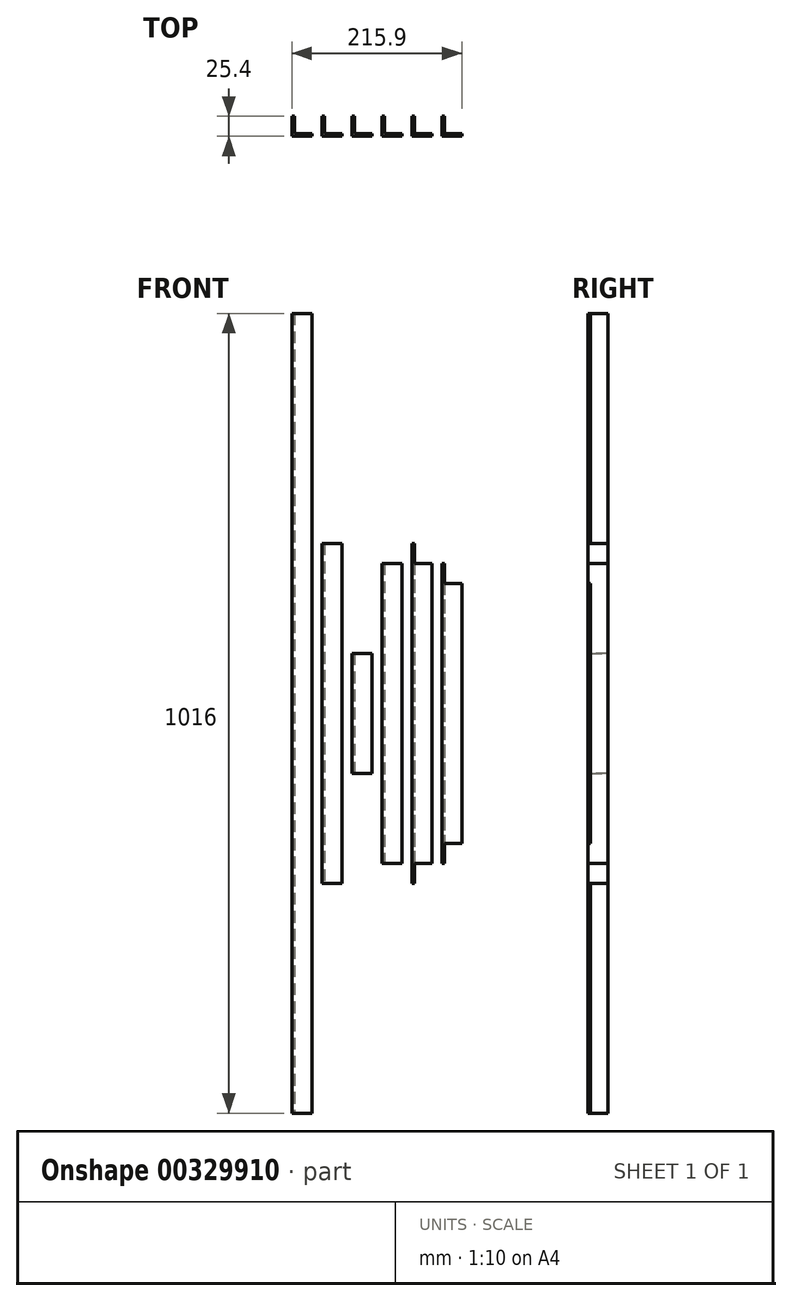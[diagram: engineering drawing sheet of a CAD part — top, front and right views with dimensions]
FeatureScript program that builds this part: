
annotation { "Feature Type Name" : "Feature", "Feature Type Description" : "" }
export const myFeature = defineFeature(function(context is Context, id is Id, definition is map)
    precondition{}
    {
        {
            var Q0;
            Q0=qCreatedBy(makeId("Top.planeOp"),FACE);
            var sketch = newSketch(context, id + "F0", { "sketchPlane" : qUnion([Q0])});
            skLineSegment(sketch, "E0", {"start": v(0, 25.4) * mm, "end": v(0, 0) * mm});
            skLineSegment(sketch, "E1", {"start": v(0, 0) * mm, "end": v(25.4, 0) * mm});
            skLineSegment(sketch, "E2", {"start": v(25.4, 0) * mm, "end": v(25.4, 3.18) * mm});
            skLineSegment(sketch, "E3", {"start": v(25.4, 3.18) * mm, "end": v(3.18, 3.17) * mm});
            skLineSegment(sketch, "E4", {"start": v(3.18, 3.17) * mm, "end": v(3.18, 25.4) * mm});
            skLineSegment(sketch, "E5", {"start": v(3.18, 25.4) * mm, "end": v(0, 25.4) * mm});
            skLineSegment(sketch, "E6.1.0.0", {"start": v(63.5, 3.18) * mm, "end": v(41.28, 3.17) * mm});
            skLineSegment(sketch, "E6.1.0.1", {"start": v(41.28, 3.17) * mm, "end": v(41.28, 25.4) * mm});
            skLineSegment(sketch, "E6.1.0.2", {"start": v(38.1, 0) * mm, "end": v(63.5, 0) * mm});
            skLineSegment(sketch, "E6.1.0.3", {"start": v(38.1, 25.4) * mm, "end": v(38.1, 0) * mm});
            skLineSegment(sketch, "E6.1.0.4", {"start": v(63.5, 0) * mm, "end": v(63.5, 3.18) * mm});
            skLineSegment(sketch, "E6.1.0.5", {"start": v(41.27, 25.4) * mm, "end": v(38.1, 25.4) * mm});
            skLineSegment(sketch, "E6.2.0.0", {"start": v(101.6, 3.18) * mm, "end": v(79.38, 3.17) * mm});
            skLineSegment(sketch, "E6.2.0.1", {"start": v(79.38, 3.17) * mm, "end": v(79.38, 25.4) * mm});
            skLineSegment(sketch, "E6.2.0.2", {"start": v(76.2, 0) * mm, "end": v(101.6, 0) * mm});
            skLineSegment(sketch, "E6.2.0.3", {"start": v(76.2, 25.4) * mm, "end": v(76.2, 0) * mm});
            skLineSegment(sketch, "E6.2.0.4", {"start": v(101.6, 0) * mm, "end": v(101.6, 3.18) * mm});
            skLineSegment(sketch, "E6.2.0.5", {"start": v(79.38, 25.4) * mm, "end": v(76.2, 25.4) * mm});
            skLineSegment(sketch, "E6.direction1", {"start": v(0, 0) * mm, "end": v(38.1, 0) * mm, "construction": true});
            skLineSegment(sketch, "E7.0.3.0", {"start": v(139.7, 3.18) * mm, "end": v(117.47, 3.17) * mm});
            skLineSegment(sketch, "E7.3.3.0", {"start": v(117.47, 3.17) * mm, "end": v(117.47, 25.4) * mm});
            skLineSegment(sketch, "E7.6.3.0", {"start": v(114.3, 0) * mm, "end": v(139.7, 0) * mm});
            skLineSegment(sketch, "E7.9.3.0", {"start": v(114.3, 25.4) * mm, "end": v(114.3, 0) * mm});
            skLineSegment(sketch, "E7.12.3.0", {"start": v(139.7, 0) * mm, "end": v(139.7, 3.18) * mm});
            skLineSegment(sketch, "E7.15.3.0", {"start": v(117.47, 25.4) * mm, "end": v(114.3, 25.4) * mm});
            skLineSegment(sketch, "E8.0.4.0", {"start": v(177.8, 3.18) * mm, "end": v(155.57, 3.17) * mm});
            skLineSegment(sketch, "E8.3.4.0", {"start": v(155.57, 3.17) * mm, "end": v(155.57, 25.4) * mm});
            skLineSegment(sketch, "E8.6.4.0", {"start": v(152.4, 0) * mm, "end": v(177.8, 0) * mm});
            skLineSegment(sketch, "E8.9.4.0", {"start": v(152.4, 25.4) * mm, "end": v(152.4, 0) * mm});
            skLineSegment(sketch, "E8.12.4.0", {"start": v(177.8, 0) * mm, "end": v(177.8, 3.18) * mm});
            skLineSegment(sketch, "E8.15.4.0", {"start": v(155.57, 25.4) * mm, "end": v(152.4, 25.4) * mm});
            skLineSegment(sketch, "E9.0.5.0", {"start": v(215.9, 3.18) * mm, "end": v(193.67, 3.17) * mm});
            skLineSegment(sketch, "E9.3.5.0", {"start": v(193.67, 3.17) * mm, "end": v(193.67, 25.4) * mm});
            skLineSegment(sketch, "E9.6.5.0", {"start": v(190.5, 0) * mm, "end": v(215.9, 0) * mm});
            skLineSegment(sketch, "E9.9.5.0", {"start": v(190.5, 25.4) * mm, "end": v(190.5, 0) * mm});
            skLineSegment(sketch, "E9.12.5.0", {"start": v(215.9, 0) * mm, "end": v(215.9, 3.18) * mm});
            skLineSegment(sketch, "E9.15.5.0", {"start": v(193.67, 25.4) * mm, "end": v(190.5, 25.4) * mm});
            skSolve(sketch);
        }
        {
            var Q0;
            Q0=makeQuery(id+"F0.imprint","IMPRINT",FACE,{"disambiguationData":[TD([[makeQuery(id+"F0.imprint","IMPRINT",EDGE,{"derivedFrom":sQuery(id+"F0.wireOp",EDGE,"E0")}),1.0]])]});
            extrude(context, id + "F1", {"entities" : qUnion([Q0]), "depth" : 1016 * mm, "symmetric" : true});
        }
        {
            var Q0;
            Q0=makeQuery(id+"F0.imprint","IMPRINT",FACE,{"disambiguationData":[TD([[makeQuery(id+"F0.imprint","IMPRINT",EDGE,{"derivedFrom":sQuery(id+"F0.wireOp",EDGE,"E6.1.0.0")}),1.0]])]});
            extrude(context, id + "F2", {"entities" : qUnion([Q0]), "depth" : 431.8 * mm, "symmetric" : true});
        }
        {
            var Q0;
            Q0=makeQuery(id+"F0.imprint","IMPRINT",FACE,{"disambiguationData":[TD([[makeQuery(id+"F0.imprint","IMPRINT",EDGE,{"derivedFrom":sQuery(id+"F0.wireOp",EDGE,"E6.2.0.0")}),1.0]])]});
            extrude(context, id + "F3", {"entities" : qUnion([Q0]), "depth" : 152.4 * mm, "symmetric" : true});
        }
        {
            var Q0;
            Q0=makeQuery(id+"F0.imprint","IMPRINT",FACE,{"disambiguationData":[TD([[makeQuery(id+"F0.imprint","IMPRINT",EDGE,{"derivedFrom":sQuery(id+"F0.wireOp",EDGE,"E7.0.3.0")}),1.0]])]});
            extrude(context, id + "F4", {"entities" : qUnion([Q0]), "depth" : 381 * mm, "symmetric" : true});
        }
        {
            var Q0;
            Q0=makeQuery(id+"F0.imprint","IMPRINT",FACE,{"disambiguationData":[TD([[makeQuery(id+"F0.imprint","IMPRINT",EDGE,{"derivedFrom":sQuery(id+"F0.wireOp",EDGE,"E8.0.4.0")}),1.0]])]});
            extrude(context, id + "F5", {"entities" : qUnion([Q0]), "depth" : 431.8 * mm, "symmetric" : true});
        }
        {
            var Q0;
            Q0=makeQuery(id+"F0.imprint","IMPRINT",FACE,{"disambiguationData":[TD([[makeQuery(id+"F0.imprint","IMPRINT",EDGE,{"derivedFrom":sQuery(id+"F0.wireOp",EDGE,"E9.0.5.0")}),1.0]])]});
            extrude(context, id + "F6", {"entities" : qUnion([Q0]), "depth" : 381 * mm, "symmetric" : true});
        }
        {
            var Q0;
            Q0=makeQuery(id+"F5.opExtrude","CAP_FACE",FACE,{"disambiguationData":[OSD([sQuery(id+"F0.wireOp",EDGE,"E8.0.4.0"),sQuery(id+"F0.wireOp",EDGE,"E8.3.4.0"),sQuery(id+"F0.wireOp",EDGE,"E8.6.4.0"),sQuery(id+"F0.wireOp",EDGE,"E8.9.4.0"),sQuery(id+"F0.wireOp",EDGE,"E8.12.4.0"),sQuery(id+"F0.wireOp",EDGE,"E8.15.4.0")])],"isStart":true});
            var sketch = newSketch(context, id + "F7", { "sketchPlane" : qUnion([Q0])});
            skLineSegment(sketch, "E10.bottom", {"start": v(155.57, -3.17) * mm, "end": v(177.8, -3.17) * mm});
            skLineSegment(sketch, "E10.top", {"start": v(155.57, 0) * mm, "end": v(177.8, 0) * mm});
            skLineSegment(sketch, "E10.left", {"start": v(155.57, -3.17) * mm, "end": v(155.57, 0) * mm});
            skLineSegment(sketch, "E10.right", {"start": v(177.8, -3.17) * mm, "end": v(177.8, 0) * mm});
            skSolve(sketch);
        }
        {
            var Q0;
            Q0=makeQuery(id+"F7.imprint","IMPRINT",FACE,{"disambiguationData":[TD([[makeQuery(id+"F7.imprint","IMPRINT",EDGE,{"derivedFrom":sQuery(id+"F7.wireOp",EDGE,"E10.bottom")}),-1.0]])]});
            extrude(context, id + "F8", {"entities" : qUnion([Q0]), "operationType" : NewBodyOperationType.REMOVE, "oppositeDirection" : true, "depth" : 25.4 * mm});
        }
        {
            var Q0;
            Q0=makeQuery(id+"F5.opExtrude","CAP_FACE",FACE,{"disambiguationData":[OSD([sQuery(id+"F0.wireOp",EDGE,"E8.0.4.0"),sQuery(id+"F0.wireOp",EDGE,"E8.3.4.0"),sQuery(id+"F0.wireOp",EDGE,"E8.6.4.0"),sQuery(id+"F0.wireOp",EDGE,"E8.9.4.0"),sQuery(id+"F0.wireOp",EDGE,"E8.12.4.0"),sQuery(id+"F0.wireOp",EDGE,"E8.15.4.0")])],"isStart":false});
            var sketch = newSketch(context, id + "F9", { "sketchPlane" : qUnion([Q0])});
            skLineSegment(sketch, "E11.bottom", {"start": v(155.57, 3.17) * mm, "end": v(177.8, 3.17) * mm});
            skLineSegment(sketch, "E11.top", {"start": v(155.57, 0) * mm, "end": v(177.8, 0) * mm});
            skLineSegment(sketch, "E11.left", {"start": v(155.57, 3.17) * mm, "end": v(155.57, 0) * mm});
            skLineSegment(sketch, "E11.right", {"start": v(177.8, 3.17) * mm, "end": v(177.8, 0) * mm});
            skSolve(sketch);
        }
        {
            var Q0;
            Q0=makeQuery(id+"F9.imprint","IMPRINT",FACE,{"disambiguationData":[TD([[makeQuery(id+"F9.imprint","IMPRINT",EDGE,{"derivedFrom":sQuery(id+"F9.wireOp",EDGE,"E11.bottom")}),1.0]])]});
            extrude(context, id + "F10", {"entities" : qUnion([Q0]), "operationType" : NewBodyOperationType.REMOVE, "oppositeDirection" : true, "depth" : 25.4 * mm});
        }
        {
            var Q0;
            Q0=makeQuery(id+"F6.opExtrude","CAP_FACE",FACE,{"disambiguationData":[OSD([sQuery(id+"F0.wireOp",EDGE,"E9.0.5.0"),sQuery(id+"F0.wireOp",EDGE,"E9.3.5.0"),sQuery(id+"F0.wireOp",EDGE,"E9.6.5.0"),sQuery(id+"F0.wireOp",EDGE,"E9.9.5.0"),sQuery(id+"F0.wireOp",EDGE,"E9.12.5.0"),sQuery(id+"F0.wireOp",EDGE,"E9.15.5.0")])],"isStart":true});
            var sketch = newSketch(context, id + "F11", { "sketchPlane" : qUnion([Q0])});
            skLineSegment(sketch, "E12.bottom", {"start": v(193.67, -3.17) * mm, "end": v(215.9, -3.17) * mm});
            skLineSegment(sketch, "E12.top", {"start": v(193.67, 0) * mm, "end": v(215.9, 0) * mm});
            skLineSegment(sketch, "E12.left", {"start": v(193.67, -3.17) * mm, "end": v(193.67, 0) * mm});
            skLineSegment(sketch, "E12.right", {"start": v(215.9, -3.17) * mm, "end": v(215.9, 0) * mm});
            skSolve(sketch);
        }
        {
            var Q0;
            Q0=makeQuery(id+"F11.imprint","IMPRINT",FACE,{"disambiguationData":[TD([[makeQuery(id+"F11.imprint","IMPRINT",EDGE,{"derivedFrom":sQuery(id+"F11.wireOp",EDGE,"E12.bottom")}),-1.0]])]});
            extrude(context, id + "F12", {"entities" : qUnion([Q0]), "operationType" : NewBodyOperationType.REMOVE, "oppositeDirection" : true, "depth" : 25.4 * mm});
        }
        {
            var Q0;
            Q0=makeQuery(id+"F6.opExtrude","CAP_FACE",FACE,{"disambiguationData":[OSD([sQuery(id+"F0.wireOp",EDGE,"E9.0.5.0"),sQuery(id+"F0.wireOp",EDGE,"E9.3.5.0"),sQuery(id+"F0.wireOp",EDGE,"E9.6.5.0"),sQuery(id+"F0.wireOp",EDGE,"E9.9.5.0"),sQuery(id+"F0.wireOp",EDGE,"E9.12.5.0"),sQuery(id+"F0.wireOp",EDGE,"E9.15.5.0")])],"isStart":false});
            var sketch = newSketch(context, id + "F13", { "sketchPlane" : qUnion([Q0])});
            skLineSegment(sketch, "E13.bottom", {"start": v(193.67, 3.17) * mm, "end": v(215.9, 3.17) * mm});
            skLineSegment(sketch, "E13.top", {"start": v(193.67, 0) * mm, "end": v(215.9, 0) * mm});
            skLineSegment(sketch, "E13.left", {"start": v(193.67, 3.17) * mm, "end": v(193.67, 0) * mm});
            skLineSegment(sketch, "E13.right", {"start": v(215.9, 3.17) * mm, "end": v(215.9, 0) * mm});
            skSolve(sketch);
        }
        {
            var Q0;
            Q0=makeQuery(id+"F13.imprint","IMPRINT",FACE,{"disambiguationData":[TD([[makeQuery(id+"F13.imprint","IMPRINT",EDGE,{"derivedFrom":sQuery(id+"F13.wireOp",EDGE,"E13.bottom")}),1.0]])]});
            extrude(context, id + "F14", {"entities" : qUnion([Q0]), "operationType" : NewBodyOperationType.REMOVE, "oppositeDirection" : true, "depth" : 25.4 * mm});
        }
    });
